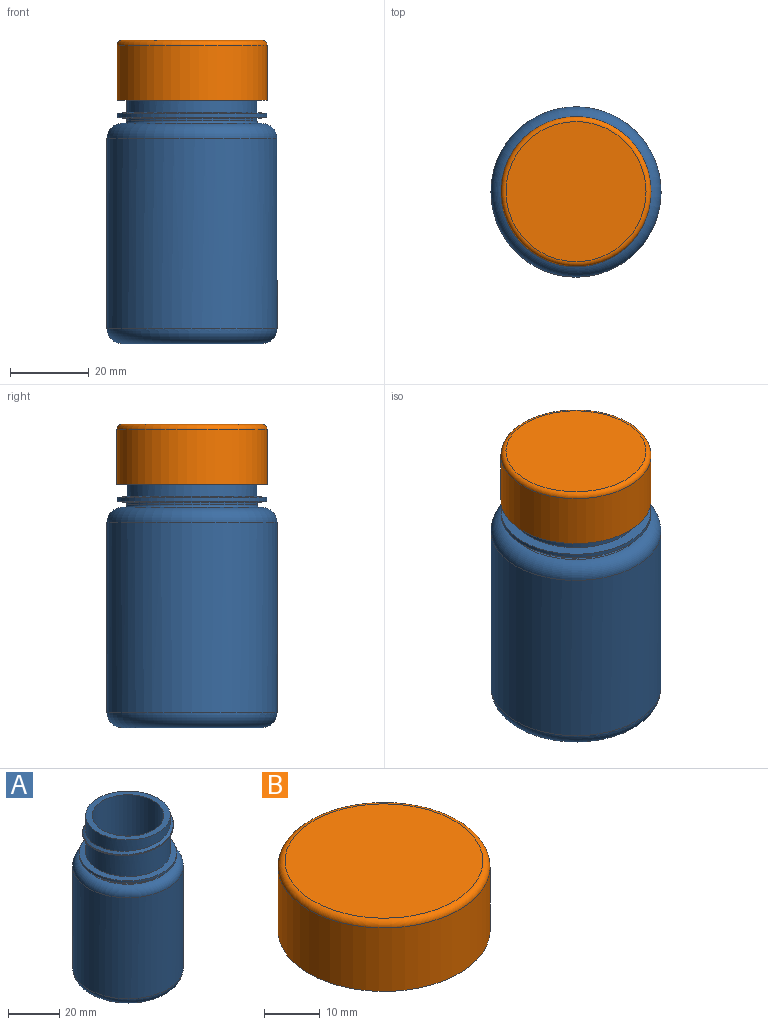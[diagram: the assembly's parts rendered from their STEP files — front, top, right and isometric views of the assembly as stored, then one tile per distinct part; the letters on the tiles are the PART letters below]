
ASSEMBLY  parts=2 mates=1
PART A: 24 faces, bbox 46.8x46.8x76.2 mm
  f0: plane 1.31x1.28mm, normal (0,1,0), area 1mm2, adj f2,f3,f4,f5
  f1: plane 1.31x1.27mm, normal (0,-1,0), area 1mm2, adj f2,f3,f4,f5
  f2: bspline ~36.58x36.58mm, area 105.4mm2, adj f0,f1,f4,f5
  f3: bspline ~36.58x36.58mm, area 149.4mm2, adj f0,f1,f4,f5
  f4: bspline ~36.58x36.58mm, area 71.3mm2, adj f0,f1,f2,f3
  f5: cylinder r=16.51mm len=33.02mm, axis (0,0,-1), area 1686.3mm2, adj f0,f1,f2,f3,f6,f16
  f6: plane 33.02x33.02mm, normal (0,0,1), area 243.2mm2, adj f5,f17
  f7: cylinder r=16.51mm len=33.02mm, axis (0,0,-1), area 65.9mm2, adj f13,f15
  f8: plane 35.56x35.56mm, normal (0,0,1), area 69.7mm2, adj f11,f13
  f9: cylinder r=21.59mm len=48.26mm, axis (0,0,-1), area 6546.7mm2, adj f11,f12
  f10: plane 35.56x35.56mm, normal (0,0,-1), area 993.1mm2, adj f12
  f11: torus R=17.78mm, axis (0,0,-1), area 759.8mm2, adj f8,f9
  f12: torus R=17.78mm, axis (0,0,1), area 759.8mm2, adj f9,f10
  f13: torus R=17.14mm, axis (0,0,-1), area 104.9mm2, adj f7,f8
  f14: cylinder r=19.04mm len=38.07mm, axis (0,0,-1), area 121.5mm2, adj f15,f16
  f15: cone r=16.51mm half-angle=84.3deg, axis (0,0,1), area 283.7mm2, adj f7,f14
  f16: cone r=19.04mm half-angle=84.3deg, axis (0,0,-1), area 283.7mm2, adj f5,f14
  f17: cylinder r=13.97mm len=27.94mm, axis (0,0,-1), area 1727.9mm2, adj f6,f23
  f18: plane 35.56x35.56mm, normal (0,0,-1), area 69.7mm2, adj f21,f23
  f19: cylinder r=19.05mm len=48.26mm, axis (0,0,-1), area 5776.5mm2, adj f21,f22
  f20: plane 35.56x35.56mm, normal (0,0,1), area 993.1mm2, adj f22
  f21: torus R=17.78mm, axis (0,0,-1), area 233mm2, adj f18,f19
  f22: torus R=17.78mm, axis (0,0,1), area 233mm2, adj f19,f20
  f23: torus R=17.14mm, axis (0,0,-1), area 473.9mm2, adj f17,f18
PART B: 10 faces, bbox 41.2x41.2x15.2 mm
  f0: plane 38.1x38.1mm, normal (0,0,-1), area 283.8mm2, adj f1,f4
  f1: cylinder r=19.05mm len=38.1mm, axis (0,0,-1), area 1672.1mm2, adj f0,f3
  f2: plane 35.56x35.56mm, normal (0,0,1), area 993.1mm2, adj f3
  f3: torus R=17.78mm, axis (0,0,-1), area 233mm2, adj f1,f2
  f4: cylinder r=16.51mm len=33.02mm, axis (0,0,-1), area 1053.9mm2, adj f0,f5,f6,f7,f8,f9
  f5: plane 33.02x33.02mm, normal (0,0,-1), area 856.3mm2, adj f4
  f6: plane 1.27x1.1mm, normal (0,1,0), area 0.7mm2, adj f4,f8,f9
  f7: plane 1.27x1.1mm, normal (0,-1,0), area 0.7mm2, adj f4,f8,f9
  f8: bspline ~33.02x33.02mm, area 127.9mm2, adj f4,f6,f7,f9
  f9: bspline ~33.02x33.02mm, area 127.9mm2, adj f4,f6,f7,f8
PLACE A t=(-18.78,16,-19.09)mm fixed
PLACE B rot(axis=(0,0,-1),180deg) t=(-18.78,16,42.63)mm
MATE cylindrical A.f5 <-> B.f1  axis (0,0,-1) through (-18.78,16,48.35)mm
